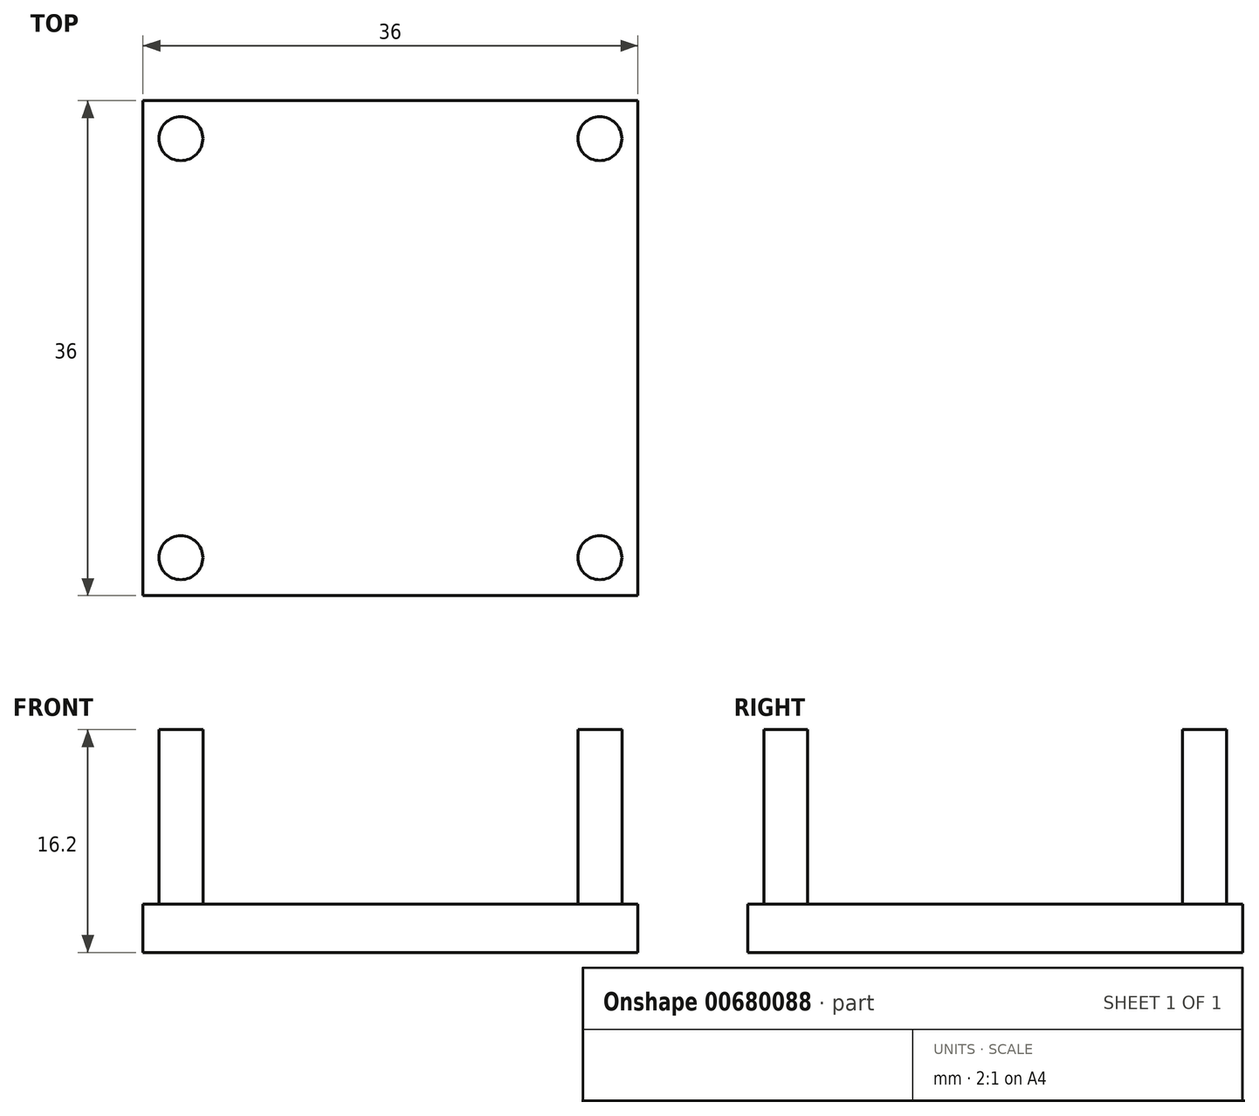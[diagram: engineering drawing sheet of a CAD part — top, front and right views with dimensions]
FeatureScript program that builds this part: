
annotation { "Feature Type Name" : "Feature", "Feature Type Description" : "" }
export const myFeature = defineFeature(function(context is Context, id is Id, definition is map)
    precondition{}
    {
        {
            var Q0;
            Q0=qCreatedBy(makeId("Top.planeOp"),FACE);
            var sketch = newSketch(context, id + "F0", { "sketchPlane" : qUnion([Q0])});
            skLineSegment(sketch, "E0.bottom", {"start": v(18, -18) * mm, "end": v(-18, -18) * mm});
            skLineSegment(sketch, "E0.top", {"start": v(18, 18) * mm, "end": v(-18, 18) * mm});
            skLineSegment(sketch, "E0.left", {"start": v(18, -18) * mm, "end": v(18, 18) * mm});
            skLineSegment(sketch, "E0.right", {"start": v(-18, -18) * mm, "end": v(-18, 18) * mm});
            skPoint(sketch, "E0.middle", {"position": v(0, 0) * mm});
            skSolve(sketch);
        }
        {
            var Q0;
            Q0=makeQuery(id+"F0.imprint","IMPRINT",FACE,{"disambiguationData":[TD([[makeQuery(id+"F0.imprint","IMPRINT",EDGE,{"derivedFrom":sQuery(id+"F0.wireOp",EDGE,"E0.bottom")}),-1.0]])]});
            extrude(context, id + "F1", {"entities" : qUnion([Q0]), "depth" : 3.5 * mm, "offsetDistance" : 25.4 * mm});
        }
        {
            var Q0;
            Q0=makeQuery(id+"F1.opExtrude","CAP_FACE",FACE,{"disambiguationData":[OSD([sQuery(id+"F0.wireOp",EDGE,"E0.bottom"),sQuery(id+"F0.wireOp",EDGE,"E0.top"),sQuery(id+"F0.wireOp",EDGE,"E0.left"),sQuery(id+"F0.wireOp",EDGE,"E0.right"),sQuery(id+"F0.wireOp",EDGE,"c9zWqgU6-ft0v-IMvR-B1vk-PQs48qQ5MZMH"),sQuery(id+"F0.wireOp",EDGE,"cadb5f79-8535-41e8-b725-741dcda25f0c0.MirrorC"),sQuery(id+"F0.wireOp",EDGE,"7ac18288-f019-43e7-abc9-cf6d2be744190.MirrorC"),sQuery(id+"F0.wireOp",EDGE,"74a9dfe4-6389-4967-852f-38b84e1f21b10.MirrorC")])],"isStart":false});
            var sketch = newSketch(context, id + "F2", { "sketchPlane" : qUnion([Q0])});
            skCircle(sketch, "E1.MirrorC", {"center": v(-15.24, 15.24) * mm, "radius": 1.6 * mm});
            skCircle(sketch, "E2.MirrorC", {"center": v(15.24, 15.24) * mm, "radius": 1.6 * mm});
            skCircle(sketch, "E3.MirrorC", {"center": v(-15.24, -15.24) * mm, "radius": 1.6 * mm});
            skCircle(sketch, "E4.MirrorC", {"center": v(15.24, -15.24) * mm, "radius": 1.6 * mm});
            skSolve(sketch);
        }
        {
            var Q0;
            Q0 = qSketchRegion(id + "F2", true);
            extrude(context, id + "F3", {"entities" : qUnion([Q0]), "operationType" : NewBodyOperationType.ADD, "depth" : 12.7 * mm, "offsetDistance" : 25.4 * mm});
        }
    });
